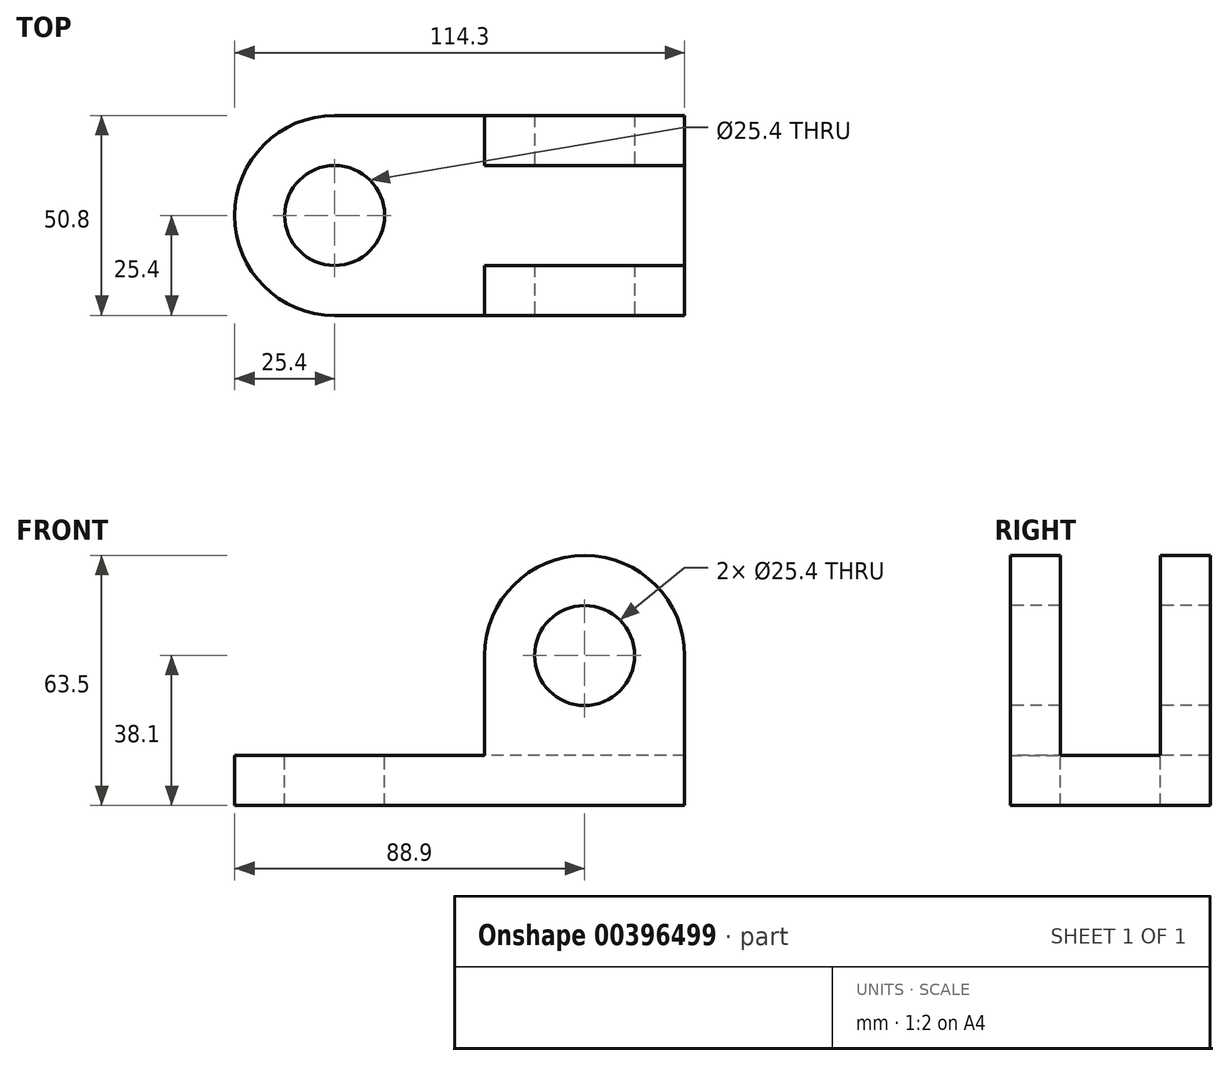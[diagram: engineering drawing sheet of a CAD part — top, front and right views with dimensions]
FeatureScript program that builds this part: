
annotation { "Feature Type Name" : "Feature", "Feature Type Description" : "" }
export const myFeature = defineFeature(function(context is Context, id is Id, definition is map)
    precondition{}
    {
        {
            var Q0;
            Q0=qCreatedBy(makeId("Top.planeOp"),FACE);
            var sketch = newSketch(context, id + "F0", { "sketchPlane" : qUnion([Q0])});
            skLineSegment(sketch, "E0.bottom", {"start": v(0, 0) * mm, "end": v(88.9, 0) * mm});
            skLineSegment(sketch, "E0.top", {"start": v(0, 50.8) * mm, "end": v(88.9, 50.8) * mm});
            skLineSegment(sketch, "E0.left", {"start": v(0, 0) * mm, "end": v(0, 50.8) * mm});
            skLineSegment(sketch, "E0.right", {"start": v(88.9, 0) * mm, "end": v(88.9, 50.8) * mm});
            skCircle(sketch, "E1", {"center": v(0, 25.4) * mm, "radius": 25.4 * mm});
            skSolve(sketch);
        }
        {
            var Q0;
            {var subQ0=sQuery(id+"F0.wireOp",EDGE,"E0.bottom");Q0=makeQuery(id+"F0.imprint","IMPRINT",FACE,{"disambiguationData":[TD([[makeQuery(id+"F0.imprint","IMPRINT",EDGE,{"derivedFrom":subQ0}),1.0]])]});}
            var Q1;
            {var subQ0=sQuery(id+"F0.wireOp",EDGE,"E0.left");Q1=makeQuery(id+"F0.imprint","IMPRINT",FACE,{"disambiguationData":[TD([[makeQuery(id+"F0.imprint","IMPRINT",EDGE,{"derivedFrom":subQ0}),-1.0]])]});}
            var Q2;
            {var subQ0=sQuery(id+"F0.wireOp",EDGE,"E0.left");Q2=makeQuery(id+"F0.imprint","IMPRINT",FACE,{"disambiguationData":[TD([[makeQuery(id+"F0.imprint","IMPRINT",EDGE,{"derivedFrom":subQ0}),1.0]])]});}
            extrude(context, id + "F1", {"entities" : qUnion([Q0, Q1, Q2]), "depth" : 12.7 * mm});
        }
        {
            var Q0;
            Q0=makeQuery(id+"F1.opExtrude","CAP_FACE",FACE,{"disambiguationData":[OSD([sQuery(id+"F0.wireOp",EDGE,"E0.bottom"),sQuery(id+"F0.wireOp",EDGE,"E0.top"),sQuery(id+"F0.wireOp",EDGE,"E0.right"),sQuery(id+"F0.wireOp",EDGE,"E1")])],"isStart":false});
            var sketch = newSketch(context, id + "F2", { "sketchPlane" : qUnion([Q0])});
            skCircle(sketch, "E2", {"center": v(0, 25.4) * mm, "radius": 12.7 * mm});
            skSolve(sketch);
        }
        {
            var Q0;
            Q0=makeQuery(id+"F2.imprint","IMPRINT",FACE,{"disambiguationData":[TD([[makeQuery(id+"F2.imprint","IMPRINT",EDGE,{"derivedFrom":sQuery(id+"F2.wireOp",EDGE,"E2")}),1.0]])]});
            extrude(context, id + "F3", {"entities" : qUnion([Q0]), "operationType" : NewBodyOperationType.REMOVE, "endBound" : BoundingType.THROUGH_ALL, "oppositeDirection" : true, "depth" : 25.4 * mm});
        }
        {
            var Q0;
            Q0=makeQuery(id+"F1.opExtrude","CAP_FACE",FACE,{"disambiguationData":[OSD([sQuery(id+"F0.wireOp",EDGE,"E0.bottom"),sQuery(id+"F0.wireOp",EDGE,"E0.top"),sQuery(id+"F0.wireOp",EDGE,"E0.right"),sQuery(id+"F0.wireOp",EDGE,"E1")])],"isStart":false});
            var sketch = newSketch(context, id + "F4", { "sketchPlane" : qUnion([Q0])});
            skLineSegment(sketch, "E3.bottom", {"start": v(88.9, 50.8) * mm, "end": v(38.1, 50.8) * mm});
            skLineSegment(sketch, "E3.top", {"start": v(88.9, 38.1) * mm, "end": v(38.1, 38.1) * mm});
            skLineSegment(sketch, "E3.left", {"start": v(88.9, 50.8) * mm, "end": v(88.9, 38.1) * mm});
            skLineSegment(sketch, "E3.right", {"start": v(38.1, 50.8) * mm, "end": v(38.1, 38.1) * mm});
            skLineSegment(sketch, "E4.bottom", {"start": v(88.9, 0) * mm, "end": v(38.1, 0) * mm});
            skLineSegment(sketch, "E4.top", {"start": v(88.9, 12.7) * mm, "end": v(38.1, 12.7) * mm});
            skLineSegment(sketch, "E4.left", {"start": v(88.9, 0) * mm, "end": v(88.9, 12.7) * mm});
            skLineSegment(sketch, "E4.right", {"start": v(38.1, 0) * mm, "end": v(38.1, 12.7) * mm});
            skSolve(sketch);
        }
        {
            var Q0;
            Q0=makeQuery(id+"F4.imprint","IMPRINT",FACE,{"disambiguationData":[TD([[makeQuery(id+"F4.imprint","IMPRINT",EDGE,{"derivedFrom":sQuery(id+"F4.wireOp",EDGE,"E3.bottom")}),-1.0]])]});
            var Q1;
            Q1=makeQuery(id+"F4.imprint","IMPRINT",FACE,{"disambiguationData":[TD([[makeQuery(id+"F4.imprint","IMPRINT",EDGE,{"derivedFrom":sQuery(id+"F4.wireOp",EDGE,"E4.bottom")}),1.0]])]});
            extrude(context, id + "F5", {"entities" : qUnion([Q0, Q1]), "operationType" : NewBodyOperationType.ADD, "depth" : 50.8 * mm});
        }
        {
            var Q0;
            Q0=makeQuery(id+"F5.boolean.opBoolean","MERGE",FACE,{"derivedFrom":[makeQuery(id+"F1.opExtrude","SWEPT_FACE",FACE,{"disambiguationData":[OSD([sQuery(id+"F0.wireOp",EDGE,"E0.bottom")])]}),makeQuery(id+"F5.opExtrude","SWEPT_FACE",FACE,{"disambiguationData":[OSD([sQuery(id+"F4.wireOp",EDGE,"E4.bottom")])]})]});
            var sketch = newSketch(context, id + "F6", { "sketchPlane" : qUnion([Q0])});
            skCircle(sketch, "E5", {"center": v(63.5, 38.1) * mm, "radius": 12.7 * mm});
            skPoint(sketch, "E5.centerSnap0", {"position": v(63.5, 63.5) * mm});
            skCircle(sketch, "E6", {"center": v(63.5, 38.1) * mm, "radius": 25.4 * mm});
            skSolve(sketch);
        }
        {
            var Q0;
            {var subQ0=sQuery(id+"F6.wireOp",EDGE,"E6");var subQ1=sQuery(id+"F4.wireOp",EDGE,"E4.bottom");var subQ2=makeQuery(id+"F5.opExtrude","CAP_EDGE",EDGE,{"disambiguationData":[OSD([subQ1])],"isStart":false});var subQ3=makeQuery(id+"F6.imprint","INTERSECT",VERTEX,{"derivedFrom":[subQ2,subQ0]});Q0=makeQuery(id+"F6.imprint","IMPRINT",FACE,{"disambiguationData":[TD([[makeQuery(id+"F6.imprint","IMPRINT",EDGE,{"disambiguationData":[TD([[subQ3,-1.0]])],"derivedFrom":subQ0}),-1.0]])]});}
            var Q1;
            {var subQ0=sQuery(id+"F6.wireOp",EDGE,"E6");var subQ1=sQuery(id+"F4.wireOp",EDGE,"E4.bottom");var subQ2=makeQuery(id+"F5.opExtrude","CAP_EDGE",EDGE,{"disambiguationData":[OSD([subQ1])],"isStart":false});var subQ3=makeQuery(id+"F6.imprint","INTERSECT",VERTEX,{"derivedFrom":[subQ2,subQ0]});Q1=makeQuery(id+"F6.imprint","IMPRINT",FACE,{"disambiguationData":[TD([[makeQuery(id+"F6.imprint","IMPRINT",EDGE,{"disambiguationData":[TD([[subQ3,1.0]])],"derivedFrom":subQ0}),-1.0]])]});}
            var Q2;
            Q2=makeQuery(id+"F6.imprint","IMPRINT",FACE,{"disambiguationData":[TD([[makeQuery(id+"F6.imprint","IMPRINT",EDGE,{"derivedFrom":sQuery(id+"F6.wireOp",EDGE,"E5")}),1.0]])]});
            extrude(context, id + "F7", {"entities" : qUnion([Q0, Q1, Q2]), "operationType" : NewBodyOperationType.REMOVE, "endBound" : BoundingType.THROUGH_ALL, "oppositeDirection" : true, "depth" : 25.4 * mm});
        }
    });
